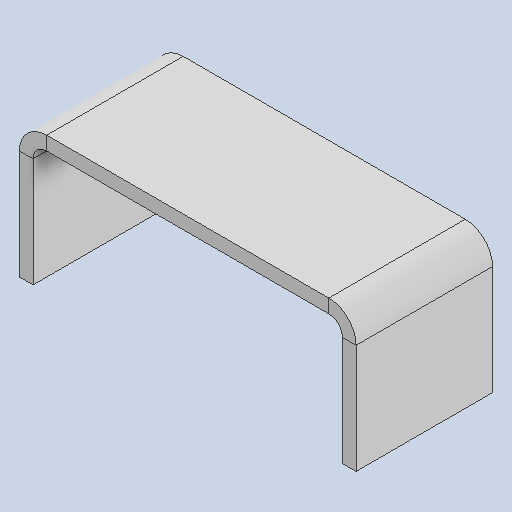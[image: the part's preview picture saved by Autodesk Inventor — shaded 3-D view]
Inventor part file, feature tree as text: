
AUTODESK INVENTOR PART (.ipt)
format: ipt  version: 2025 (Build 290162010, 162A)  size: 117,248 bytes
history: native  units: mm
features: sheet_metal_op x3, sketch x1, other x1
ambient origin geometry x8: Origin, YZ Plane, XZ Plane, XY Plane, X Axis, Y Axis, Z Axis, Center Point
bodies: Solid1 (feature_tree)
feature tree (5):
  sheet_metal_op  "Contour Flange1"
  sketch  "Sketch1"  dims[d0=30.0mm d1=74.0mm d4=3.0mm d5=3.0mm d6=1.5mm d7=6.0mm d8=3.0mm d9=30.0mm d10=3.0mm d11=3.048mm d12=12.0mm d13=3.0mm d14=3.0mm]
  other  "Plate1"
  sheet_metal_op  "Bend1"
  sheet_metal_op  "Corner1"
